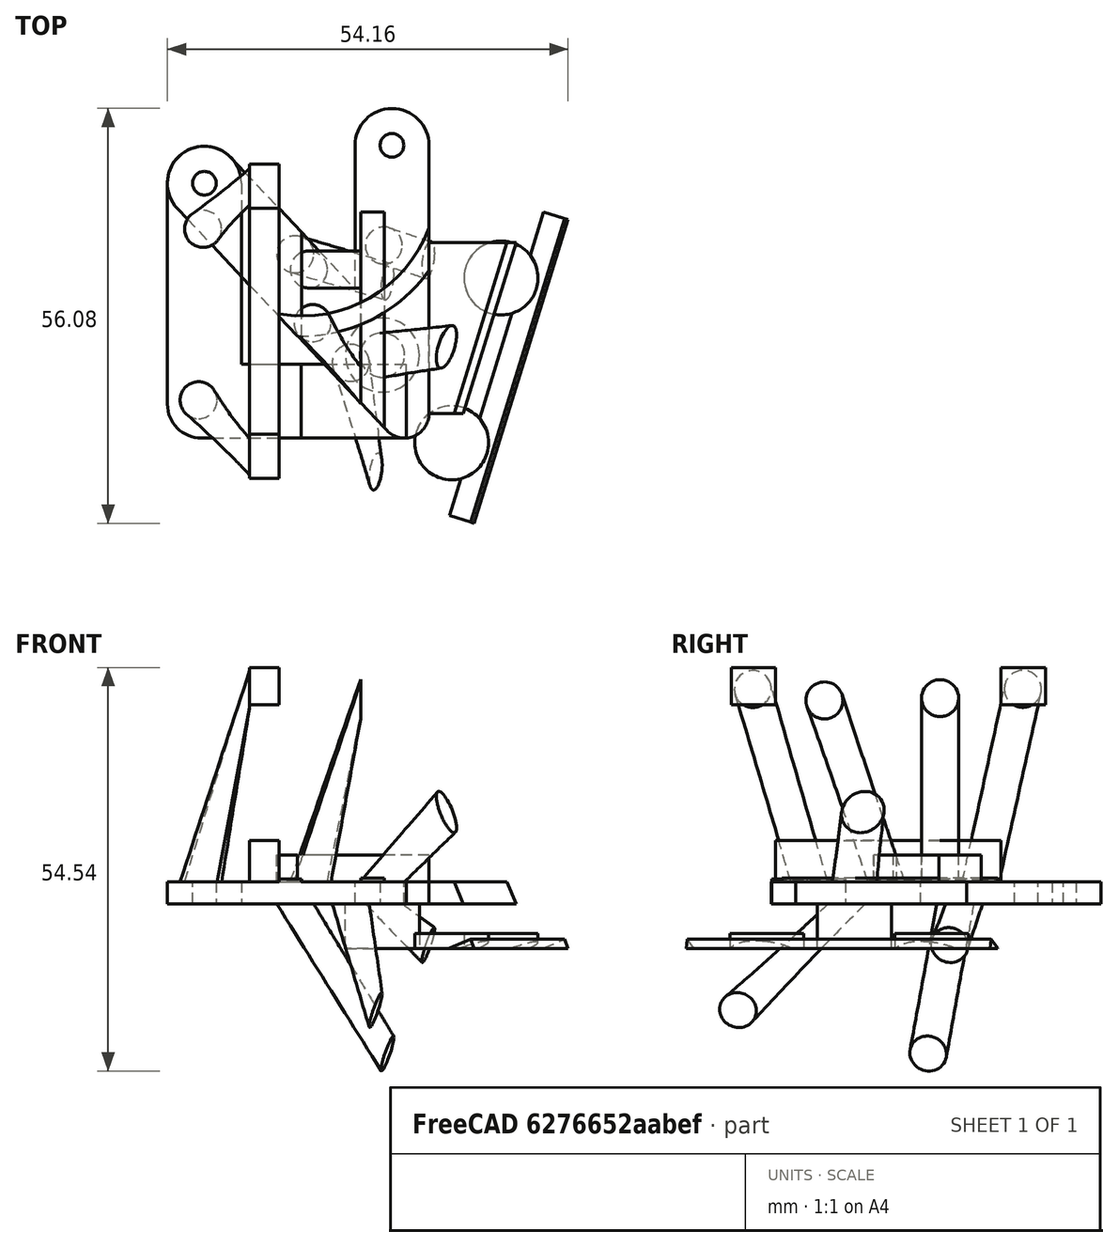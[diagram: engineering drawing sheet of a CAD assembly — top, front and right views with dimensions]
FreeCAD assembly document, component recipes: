
FREECAD ASSEMBLY — COMPONENT RECIPES ("left-thumb-mount")

This assembly document has 6 components, labeled P0..P5 below (a component is one placed body or linked part). 3 of them carry a construction recipe — the FreeCAD feature program that regenerates the part from scratch, quoted from this document or its linked companion documents; the rest are supplied as boundary geometry only. No exploded tour is included for this assembly.
COMPONENT P0 — recipe-attached ("case", modeled in this document).
Construction recipe (the document's own serialized feature program — sketch geometry with constraints, then the solid features built on it; lengths are millimeters unless a unit is written):

FEATURE [PartDesign::SubShapeBinder] Binder020
  BindCopyOnChange = 0
  BindMode = 0
  ClaimChildren = false
  Context = -> Part002 [Part001.Body.Binder020.]
  Fuse = false
  MakeFace = true
  OffsetFill = false
  OffsetIntersection = false
  OffsetJoinType = 0
  OffsetOpenResult = false
  PartialLoad = false
  Refine = true
  Relative = true
  Support = -> [Link026[Pad047.Face11]]
  _Version = 2
FEATURE [PartDesign::SubShapeBinder] Binder021
  BindCopyOnChange = 0
  BindMode = 0
  ClaimChildren = false
  Context = -> Part002 [Part001.Body.Binder021.]
  Fuse = false
  MakeFace = true
  OffsetFill = false
  OffsetIntersection = false
  OffsetJoinType = 0
  OffsetOpenResult = false
  PartialLoad = false
  Refine = true
  Relative = true
  Support = -> [Link027[Face4]]
  _Version = 2
FEATURE [Sketcher::SketchObject] Sketch091
  ArcFitTolerance = 1e-06
  AttachmentSupport = -> [Binder021]
  ExternalGeometry = -> [Binder021]
  FullyConstrained = false
  MakeInternals = false
  MapMode = 5
  Placement = pos=(0,0,5) rot=(1,0,0;3.14159rad)
  sketch-geometry (4):
    g0: ArcOfCircle CenterX=62 CenterY=1 CenterZ=0 NormalX=0 NormalY=0 NormalZ=1 AngleXU=0 Radius=21.0029 StartAngle=0.616798 EndAngle=1.60102
    g1: ArcOfCircle CenterX=62 CenterY=1 CenterZ=0 NormalX=0 NormalY=0 NormalZ=1 AngleXU=0 Radius=18.3 StartAngle=0.35909 EndAngle=1.76369
    g2: LineSegment StartX=79.1328 StartY=13.1486 StartZ=0 EndX=79.1328 EndY=7.43104 EndZ=0
    g3: LineSegment StartX=58.4919 StartY=18.9606 StartZ=0 EndX=61.3652 EndY=21.9933 EndZ=0
  constraints (6):
    c: Coincident(g1,g-4)
    c: Coincident(g2,g0)
    c: Coincident(g2,g1)
    c: Vertical(g2)
    c: Coincident(g3,g1)
    c: Coincident(g3,g0)
FEATURE [PartDesign::Pad] Pad054
  Direction = (0,0,-1)
  Length = 10
  Length2 = 10
  Profile = -> Sketch091
  ReferenceAxis = -> Sketch091 [N_Axis]
  Refine = true
  Suppressed = false
  Type = 3
  UpToFace = -> Binder020 [Face1]
FEATURE [PartDesign::SubShapeBinder] Binder022
  BindCopyOnChange = 0
  BindMode = 0
  ClaimChildren = false
  Context = -> Part002 [Part001.Body.Binder022.]
  Fuse = false
  MakeFace = true
  OffsetFill = false
  OffsetIntersection = false
  OffsetJoinType = 0
  OffsetOpenResult = false
  PartialLoad = false
  Refine = true
  Relative = true
  Support = -> [Link010[Chamfer001.Face3]]
  _Version = 2
FEATURE [PartDesign::SubShapeBinder] Binder023
  BindCopyOnChange = 0
  BindMode = 0
  ClaimChildren = false
  Context = -> Part002 [Part001.Body.Binder023.]
  Fuse = false
  MakeFace = true
  OffsetFill = false
  OffsetIntersection = false
  OffsetJoinType = 0
  OffsetOpenResult = false
  PartialLoad = false
  Refine = true
  Relative = true
  Support = -> [Link006[Body002.Chamfer.Face1]]
  _Version = 2
FEATURE [PartDesign::Plane] DatumPlane001
  AttachmentSupport = -> [Binder023]
  Length = 182.676
  MapMode = 5
  Placement = pos=(0,0,-7.6) rot=(1,0,0;3.14159rad)
  ResizeMode = 0
  Width = 128.706
FEATURE [PartDesign::Pad] Pad055
  BaseFeature = -> Pad054
  Direction = (0.346621,-0.107166,-0.931863)
  Length = 10
  Length2 = 10
  Profile = -> Binder022 [Face1]
  Refine = true
  Suppressed = false
  Type = 3
  UpToFace = -> DatumPlane001
FEATURE [PartDesign::SubShapeBinder] Binder024
  BindCopyOnChange = 0
  BindMode = 0
  ClaimChildren = false
  Context = -> Part002 [Part001.Body.Binder024.]
  Fuse = false
  MakeFace = true
  OffsetFill = false
  OffsetIntersection = false
  OffsetJoinType = 0
  OffsetOpenResult = false
  PartialLoad = false
  Refine = true
  Relative = true
  Support = -> [Link010[Chamfer001.Face1]]
  _Version = 2
FEATURE [PartDesign::SubShapeBinder] Binder025
  BindCopyOnChange = 0
  BindMode = 0
  ClaimChildren = false
  Context = -> Part002 [Part001.Body.Binder025.]
  Fuse = false
  MakeFace = true
  OffsetFill = false
  OffsetIntersection = false
  OffsetJoinType = 0
  OffsetOpenResult = false
  PartialLoad = false
  Refine = true
  Relative = true
  Support = -> [Link026[Pad047.Face5]]
  _Version = 2
FEATURE [Sketcher::SketchObject] Sketch092
  ArcFitTolerance = 1e-06
  AttachmentSupport = -> [Binder025]
  ExternalGeometry = -> [Binder025]
  FullyConstrained = false
  MakeInternals = false
  MapMode = 5
  Placement = pos=(79.1219,0,0) rot=(0.57735,0.57735,0.57735;2.0944rad)
  sketch-geometry (4):
    g0: LineSegment StartX=-32.5119 StartY=1.4 StartZ=0 EndX=-32.5119 EndY=-1.6 EndZ=0
    g1: LineSegment StartX=-32.5119 StartY=-1.6 StartZ=0 EndX=-9.39731 EndY=-1.6 EndZ=0
    g2: LineSegment StartX=-9.39731 StartY=-1.6 StartZ=0 EndX=-9.39731 EndY=1.4 EndZ=0
    g3: LineSegment StartX=-9.39731 StartY=1.4 StartZ=0 EndX=-32.5119 EndY=1.4 EndZ=0
  constraints (10):
    c: Coincident(g0,g1)
    c: Coincident(g1,g2)
    c: Coincident(g2,g3)
    c: Coincident(g3,g0)
    c: Vertical(g0)
    c: Vertical(g2)
    c: Horizontal(g1)
    c: Horizontal(g3)
    c: Coincident(g0,g-3)
    c: PointOnObject(g1,g-4)
FEATURE [PartDesign::Pad] Pad056
  BaseFeature = -> Pad055
  Direction = (1,0,0)
  Length = 10
  Length2 = 10
  Profile = -> Sketch092
  ReferenceAxis = -> Sketch092 [N_Axis]
  Refine = true
  Suppressed = false
  Type = 3
  UpToFace = -> Binder024 [Face1]
FEATURE [Sketcher::SketchObject] Sketch093
  ArcFitTolerance = 1e-06
  AttachmentSupport = -> [Binder020]
  FullyConstrained = false
  MakeInternals = false
  MapMode = 5
  Placement = pos=(0,0,1.4) rot=(0,0,1;0rad)
  sketch-geometry (1):
    g0: Circle CenterX=72.8287 CenterY=-24.5846 CenterZ=0 NormalX=0 NormalY=0 NormalZ=1 AngleXU=0 Radius=3
  constraints (1):
    c: Diameter(g0) = 6
FEATURE [Sketcher::SketchObject] Sketch094
  ArcFitTolerance = 1e-06
  AttachmentSupport = -> [Binder024]
  FullyConstrained = false
  MakeInternals = false
  MapMode = 5
  Placement = pos=(73.8171,-22.8543,30.0857) rot=(-0.55329,0.66874,0.496645;3.76991rad)
  sketch-geometry (1):
    g0: Circle CenterX=0.63341 CenterY=-20.7385 CenterZ=0 NormalX=0 NormalY=0 NormalZ=1 AngleXU=0 Radius=3
  constraints (1):
    c: Diameter(g0) = 6
FEATURE [PartDesign::AdditiveLoft] AdditiveLoft012
  BaseFeature = -> Pad056
  Closed = false
  Profile = -> Sketch093
  Refine = true
  Ruled = false
  Sections = -> [Sketch094]
  Suppressed = false
FEATURE [PartDesign::SubShapeBinder] Binder026
  BindCopyOnChange = 0
  BindMode = 0
  ClaimChildren = false
  Context = -> Part002 [Part001.Body.Binder026.]
  Fuse = false
  MakeFace = true
  OffsetFill = false
  OffsetIntersection = false
  OffsetJoinType = 0
  OffsetOpenResult = false
  PartialLoad = false
  Refine = true
  Relative = true
  Support = -> [Link026[Pad047.Face10]]
  _Version = 2
FEATURE [Sketcher::SketchObject] Sketch095
  ArcFitTolerance = 1e-06
  AttachmentSupport = -> [Binder026]
  FullyConstrained = false
  MakeInternals = false
  MapMode = 5
  Placement = pos=(0,0,-1.6) rot=(1,0,0;3.14159rad)
  sketch-geometry (1):
    g0: Circle CenterX=72.8282 CenterY=24.5928 CenterZ=0 NormalX=0 NormalY=0 NormalZ=1 AngleXU=0 Radius=5
  constraints (1):
    c: Diameter(g0) = 10
FEATURE [PartDesign::Pad] Pad057
  BaseFeature = -> AdditiveLoft012
  Direction = (0,0,-1)
  Length = 10
  Length2 = 10
  Profile = -> Sketch095
  ReferenceAxis = -> Sketch095 [N_Axis]
  Refine = true
  Suppressed = false
  Type = 3
  UpToFace = -> DatumPlane001 [Plane]
FEATURE [Sketcher::SketchObject] Sketch096
  ArcFitTolerance = 1e-06
  AttachmentSupport = -> [DatumPlane001]
  FullyConstrained = false
  MakeInternals = false
  MapMode = 5
  Placement = pos=(0,0,-7.6) rot=(1,0,0;3.14159rad)
  sketch-geometry (2):
    g0: Circle CenterX=82.1937 CenterY=36.4466 CenterZ=0 NormalX=0 NormalY=0 NormalZ=1 AngleXU=0 Radius=5
    g1: Circle CenterX=88.8672 CenterY=14.1556 CenterZ=0 NormalX=0 NormalY=0 NormalZ=1 AngleXU=0 Radius=5
  constraints (2):
    c: Diameter(g0) = 10
    c: Diameter(g1) = 10
FEATURE [PartDesign::Pad] Pad058
  BaseFeature = -> Pad057
  Direction = (0,0,-1)
  Length = 2
  Length2 = 10
  Profile = -> Sketch096
  ReferenceAxis = -> Sketch096 [N_Axis]
  Refine = true
  Reversed = true
  Suppressed = false
  Type = 0
FEATURE [PartDesign::Body] Body
  AllowCompound = true
  Group = -> [Binder020,Binder021,Sketch091,Pad054,Binder022,Binder023,DatumPlane001,Pad055,Binder024,Binder025,Sketch092,Pad056,Sketch093,Sketch094,AdditiveLoft012,Binder026,Sketch095,Pad057,Sketch096,Pad058]
  Origin = -> Origin019
  Tip = -> Pad058
COMPONENT P1 — geometry summary ("left"; no construction recipe available for this part):
  bounding box: 126.7 x 48.0 x 12.9 mm
  tessellated surface: 118,052 triangles
  volume: 8489 mm^3 (11% of its bounding box)
COMPONENT P2 — recipe-attached ("trackball top", modeled in this document).
Construction recipe (the document's own serialized feature program — sketch geometry with constraints, then the solid features built on it; lengths are millimeters unless a unit is written):

FEATURE [PartDesign::SubShapeBinder] Binder007
  BindCopyOnChange = 0
  BindMode = 0
  ClaimChildren = false
  Context = -> Part [Part004.Body006.Binder007.]
  Fuse = false
  MakeFace = true
  OffsetFill = false
  OffsetIntersection = false
  OffsetJoinType = 0
  OffsetOpenResult = false
  PartialLoad = false
  Refine = true
  Relative = true
  Support = -> [Link006[Body002.Chamfer.Face35,Body002.Chamfer.Face36,Body002.Chamfer.Edge24,Body002.Chamfer.Edge25]]
  _Version = 2
FEATURE [Sketcher::SketchObject] Sketch063
  ArcFitTolerance = 1e-06
  AttachmentSupport = -> [Binder007]
  ExternalGeometry = -> [Binder007]
  FullyConstrained = false
  MakeInternals = false
  MapMode = 5
  Placement = pos=(0,0,-1.6) rot=(0,0,1;0rad)
  sketch-geometry (10):
    g0: Circle CenterX=74.1219 CenterY=3.76462 CenterZ=0 NormalX=0 NormalY=0 NormalZ=1 AngleXU=0 Radius=1.6
    g1: ArcOfCircle CenterX=48.7566 CenterY=-1.349 CenterZ=0 NormalX=0 NormalY=0 NormalZ=1 AngleXU=0 Radius=5 StartAngle=0.756705 EndAngle=3.8983
    g2: Circle CenterX=48.7566 CenterY=-1.349 CenterZ=0 NormalX=0 NormalY=0 NormalZ=1 AngleXU=0 Radius=1.6
    g3: ArcOfCircle CenterX=74.1219 CenterY=3.75859 CenterZ=0 NormalX=0 NormalY=0 NormalZ=1 AngleXU=0 Radius=5 StartAngle=1e-16 EndAngle=3.14159
    g4: LineSegment StartX=69.1219 StartY=-15.6348 StartZ=0 EndX=69.1219 EndY=3.75859 EndZ=0
    g5: LineSegment StartX=79.1219 StartY=3.75859 StartZ=0 EndX=79.1219 EndY=-32.5119 EndZ=0
    g6: LineSegment StartX=45.1211 StartY=-4.78165 StartZ=0 EndX=73.4375 EndY=-34.7715 EndZ=0
    g7: LineSegment StartX=52.3921 StartY=2.08365 StartZ=0 EndX=69.1219 EndY=-15.6348 EndZ=0
    g8: ArcOfCircle CenterX=75.8306 CenterY=-32.5119 CenterZ=0 NormalX=0 NormalY=0 NormalZ=1 AngleXU=0 Radius=3.2913 StartAngle=3.8983 EndAngle=6.28319
    g9: GeomPoint [constr] X=79.1219 Y=-40.7918 Z=0
  constraints (20):
    c: Diameter(g0) = 3.2
    c: Radius(g1) = 5
    c: Angle(g1) = 3.14159
    c: Coincident(g1,g-4)
    c: Diameter(g2) = 3.2
    c: Coincident(g2,g1)
    c: Radius(g3) = 5
    c: Angle(g3) = 3.14159
    c: Coincident(g3,g-3)
    c: Coincident(g4,g3)
    c: Vertical(g4)
    c: Tangent(g3,g5) = 1.5708
    c: Vertical(g5)
    c: Tangent(g1,g6) = -1.5708
    c: Tangent(g1,g7) = 1.5708
    c: Coincident(g4,g7)
    c: PointOnObject(g9,g5)
    c: PointOnObject(g9,g6)
    c: Tangent(g5,g8) = 1.5708
    c: Tangent(g6,g8) = -1.5708
FEATURE [PartDesign::Pad] Pad047
  Direction = (0,0,1)
  Length = 3
  Length2 = 10
  Profile = -> Sketch063
  ReferenceAxis = -> Sketch063 [N_Axis]
  Refine = true
  Suppressed = false
  Type = 0
FEATURE [PartDesign::Body] Body006  label="new mount"
  AllowCompound = false
  Group = -> [Binder007,Sketch063,Pad047]
  Origin = -> Origin013
  Tip = -> Pad047
COMPONENT P3 — geometry summary ("top-btu"; no construction recipe available for this part):
  bounding box: 43.4 x 41.1 x 21.1 mm
  tessellated surface: 85,176 triangles
  volume: 7395 mm^3 (20% of its bounding box)
COMPONENT P4 — recipe-attached ("xring", modeled in this document).
Construction recipe (the document's own serialized feature program — sketch geometry with constraints, then the solid features built on it; lengths are millimeters unless a unit is written):

FEATURE [PartDesign::SubShapeBinder] Binder020
  BindCopyOnChange = 0
  BindMode = 0
  ClaimChildren = false
  Context = -> Part002 [Part001.Body.Binder020.]
  Fuse = false
  MakeFace = true
  OffsetFill = false
  OffsetIntersection = false
  OffsetJoinType = 0
  OffsetOpenResult = false
  PartialLoad = false
  Refine = true
  Relative = true
  Support = -> [Link026[Pad047.Face11]]
  _Version = 2
FEATURE [PartDesign::SubShapeBinder] Binder021
  BindCopyOnChange = 0
  BindMode = 0
  ClaimChildren = false
  Context = -> Part002 [Part001.Body.Binder021.]
  Fuse = false
  MakeFace = true
  OffsetFill = false
  OffsetIntersection = false
  OffsetJoinType = 0
  OffsetOpenResult = false
  PartialLoad = false
  Refine = true
  Relative = true
  Support = -> [Link027[Face4]]
  _Version = 2
FEATURE [Sketcher::SketchObject] Sketch091
  ArcFitTolerance = 1e-06
  AttachmentSupport = -> [Binder021]
  ExternalGeometry = -> [Binder021]
  FullyConstrained = false
  MakeInternals = false
  MapMode = 5
  Placement = pos=(0,0,5) rot=(1,0,0;3.14159rad)
  sketch-geometry (4):
    g0: ArcOfCircle CenterX=62 CenterY=1 CenterZ=0 NormalX=0 NormalY=0 NormalZ=1 AngleXU=0 Radius=21.0029 StartAngle=0.616798 EndAngle=1.60102
    g1: ArcOfCircle CenterX=62 CenterY=1 CenterZ=0 NormalX=0 NormalY=0 NormalZ=1 AngleXU=0 Radius=18.3 StartAngle=0.35909 EndAngle=1.76369
    g2: LineSegment StartX=79.1328 StartY=13.1486 StartZ=0 EndX=79.1328 EndY=7.43104 EndZ=0
    g3: LineSegment StartX=58.4919 StartY=18.9606 StartZ=0 EndX=61.3652 EndY=21.9933 EndZ=0
  constraints (6):
    c: Coincident(g1,g-4)
    c: Coincident(g2,g0)
    c: Coincident(g2,g1)
    c: Vertical(g2)
    c: Coincident(g3,g1)
    c: Coincident(g3,g0)
FEATURE [PartDesign::Pad] Pad054
  Direction = (0,0,-1)
  Length = 10
  Length2 = 10
  Profile = -> Sketch091
  ReferenceAxis = -> Sketch091 [N_Axis]
  Refine = true
  Suppressed = false
  Type = 3
  UpToFace = -> Binder020 [Face1]
FEATURE [PartDesign::SubShapeBinder] Binder022
  BindCopyOnChange = 0
  BindMode = 0
  ClaimChildren = false
  Context = -> Part002 [Part001.Body.Binder022.]
  Fuse = false
  MakeFace = true
  OffsetFill = false
  OffsetIntersection = false
  OffsetJoinType = 0
  OffsetOpenResult = false
  PartialLoad = false
  Refine = true
  Relative = true
  Support = -> [Link010[Chamfer001.Face3]]
  _Version = 2
FEATURE [PartDesign::SubShapeBinder] Binder023
  BindCopyOnChange = 0
  BindMode = 0
  ClaimChildren = false
  Context = -> Part002 [Part001.Body.Binder023.]
  Fuse = false
  MakeFace = true
  OffsetFill = false
  OffsetIntersection = false
  OffsetJoinType = 0
  OffsetOpenResult = false
  PartialLoad = false
  Refine = true
  Relative = true
  Support = -> [Link006[Body002.Chamfer.Face1]]
  _Version = 2
FEATURE [PartDesign::Plane] DatumPlane001
  AttachmentSupport = -> [Binder023]
  Length = 182.676
  MapMode = 5
  Placement = pos=(0,0,-7.6) rot=(1,0,0;3.14159rad)
  ResizeMode = 0
  Width = 128.706
FEATURE [PartDesign::Pad] Pad055
  BaseFeature = -> Pad054
  Direction = (0.346621,-0.107166,-0.931863)
  Length = 10
  Length2 = 10
  Profile = -> Binder022 [Face1]
  Refine = true
  Suppressed = false
  Type = 3
  UpToFace = -> DatumPlane001
FEATURE [PartDesign::SubShapeBinder] Binder024
  BindCopyOnChange = 0
  BindMode = 0
  ClaimChildren = false
  Context = -> Part002 [Part001.Body.Binder024.]
  Fuse = false
  MakeFace = true
  OffsetFill = false
  OffsetIntersection = false
  OffsetJoinType = 0
  OffsetOpenResult = false
  PartialLoad = false
  Refine = true
  Relative = true
  Support = -> [Link010[Chamfer001.Face1]]
  _Version = 2
FEATURE [PartDesign::SubShapeBinder] Binder025
  BindCopyOnChange = 0
  BindMode = 0
  ClaimChildren = false
  Context = -> Part002 [Part001.Body.Binder025.]
  Fuse = false
  MakeFace = true
  OffsetFill = false
  OffsetIntersection = false
  OffsetJoinType = 0
  OffsetOpenResult = false
  PartialLoad = false
  Refine = true
  Relative = true
  Support = -> [Link026[Pad047.Face5]]
  _Version = 2
FEATURE [Sketcher::SketchObject] Sketch092
  ArcFitTolerance = 1e-06
  AttachmentSupport = -> [Binder025]
  ExternalGeometry = -> [Binder025]
  FullyConstrained = false
  MakeInternals = false
  MapMode = 5
  Placement = pos=(79.1219,0,0) rot=(0.57735,0.57735,0.57735;2.0944rad)
  sketch-geometry (4):
    g0: LineSegment StartX=-32.5119 StartY=1.4 StartZ=0 EndX=-32.5119 EndY=-1.6 EndZ=0
    g1: LineSegment StartX=-32.5119 StartY=-1.6 StartZ=0 EndX=-9.39731 EndY=-1.6 EndZ=0
    g2: LineSegment StartX=-9.39731 StartY=-1.6 StartZ=0 EndX=-9.39731 EndY=1.4 EndZ=0
    g3: LineSegment StartX=-9.39731 StartY=1.4 StartZ=0 EndX=-32.5119 EndY=1.4 EndZ=0
  constraints (10):
    c: Coincident(g0,g1)
    c: Coincident(g1,g2)
    c: Coincident(g2,g3)
    c: Coincident(g3,g0)
    c: Vertical(g0)
    c: Vertical(g2)
    c: Horizontal(g1)
    c: Horizontal(g3)
    c: Coincident(g0,g-3)
    c: PointOnObject(g1,g-4)
FEATURE [PartDesign::Pad] Pad056
  BaseFeature = -> Pad055
  Direction = (1,0,0)
  Length = 10
  Length2 = 10
  Profile = -> Sketch092
  ReferenceAxis = -> Sketch092 [N_Axis]
  Refine = true
  Suppressed = false
  Type = 3
  UpToFace = -> Binder024 [Face1]
FEATURE [Sketcher::SketchObject] Sketch093
  ArcFitTolerance = 1e-06
  AttachmentSupport = -> [Binder020]
  FullyConstrained = false
  MakeInternals = false
  MapMode = 5
  Placement = pos=(0,0,1.4) rot=(0,0,1;0rad)
  sketch-geometry (1):
    g0: Circle CenterX=72.8287 CenterY=-24.5846 CenterZ=0 NormalX=0 NormalY=0 NormalZ=1 AngleXU=0 Radius=3
  constraints (1):
    c: Diameter(g0) = 6
FEATURE [Sketcher::SketchObject] Sketch094
  ArcFitTolerance = 1e-06
  AttachmentSupport = -> [Binder024]
  FullyConstrained = false
  MakeInternals = false
  MapMode = 5
  Placement = pos=(73.8171,-22.8543,30.0857) rot=(-0.55329,0.66874,0.496645;3.76991rad)
  sketch-geometry (1):
    g0: Circle CenterX=0.63341 CenterY=-20.7385 CenterZ=0 NormalX=0 NormalY=0 NormalZ=1 AngleXU=0 Radius=3
  constraints (1):
    c: Diameter(g0) = 6
FEATURE [PartDesign::AdditiveLoft] AdditiveLoft012
  BaseFeature = -> Pad056
  Closed = false
  Profile = -> Sketch093
  Refine = true
  Ruled = false
  Sections = -> [Sketch094]
  Suppressed = false
FEATURE [PartDesign::SubShapeBinder] Binder026
  BindCopyOnChange = 0
  BindMode = 0
  ClaimChildren = false
  Context = -> Part002 [Part001.Body.Binder026.]
  Fuse = false
  MakeFace = true
  OffsetFill = false
  OffsetIntersection = false
  OffsetJoinType = 0
  OffsetOpenResult = false
  PartialLoad = false
  Refine = true
  Relative = true
  Support = -> [Link026[Pad047.Face10]]
  _Version = 2
FEATURE [Sketcher::SketchObject] Sketch095
  ArcFitTolerance = 1e-06
  AttachmentSupport = -> [Binder026]
  FullyConstrained = false
  MakeInternals = false
  MapMode = 5
  Placement = pos=(0,0,-1.6) rot=(1,0,0;3.14159rad)
  sketch-geometry (1):
    g0: Circle CenterX=72.8282 CenterY=24.5928 CenterZ=0 NormalX=0 NormalY=0 NormalZ=1 AngleXU=0 Radius=5
  constraints (1):
    c: Diameter(g0) = 10
FEATURE [PartDesign::Pad] Pad057
  BaseFeature = -> AdditiveLoft012
  Direction = (0,0,-1)
  Length = 10
  Length2 = 10
  Profile = -> Sketch095
  ReferenceAxis = -> Sketch095 [N_Axis]
  Refine = true
  Suppressed = false
  Type = 3
  UpToFace = -> DatumPlane001 [Plane]
FEATURE [Sketcher::SketchObject] Sketch096
  ArcFitTolerance = 1e-06
  AttachmentSupport = -> [DatumPlane001]
  FullyConstrained = false
  MakeInternals = false
  MapMode = 5
  Placement = pos=(0,0,-7.6) rot=(1,0,0;3.14159rad)
  sketch-geometry (2):
    g0: Circle CenterX=82.1937 CenterY=36.4466 CenterZ=0 NormalX=0 NormalY=0 NormalZ=1 AngleXU=0 Radius=5
    g1: Circle CenterX=88.8672 CenterY=14.1556 CenterZ=0 NormalX=0 NormalY=0 NormalZ=1 AngleXU=0 Radius=5
  constraints (2):
    c: Diameter(g0) = 10
    c: Diameter(g1) = 10
FEATURE [PartDesign::Pad] Pad058
  BaseFeature = -> Pad057
  Direction = (0,0,-1)
  Length = 2
  Length2 = 10
  Profile = -> Sketch096
  ReferenceAxis = -> Sketch096 [N_Axis]
  Refine = true
  Reversed = true
  Suppressed = false
  Type = 0
FEATURE [PartDesign::Body] Body
  AllowCompound = true
  Group = -> [Binder020,Binder021,Sketch091,Pad054,Binder022,Binder023,DatumPlane001,Pad055,Binder024,Binder025,Sketch092,Pad056,Sketch093,Sketch094,AdditiveLoft012,Binder026,Sketch095,Pad057,Sketch096,Pad058]
  Origin = -> Origin019
  Tip = -> Pad058
COMPONENT P5 — geometry summary ("thumbstick"; no construction recipe available for this part):
  bounding box: 36.6 x 30.8 x 27.5 mm
  tessellated surface: 31,462 triangles
  volume: 5351 mm^3 (17% of its bounding box)
PROVENANCE & LICENSES
A FreeCAD (.FCStd) document from a public repository crawl; recipes are the document's own serialized feature recipes (and, for linked parts, companion documents' recipes).
License: gpl-3.0.
